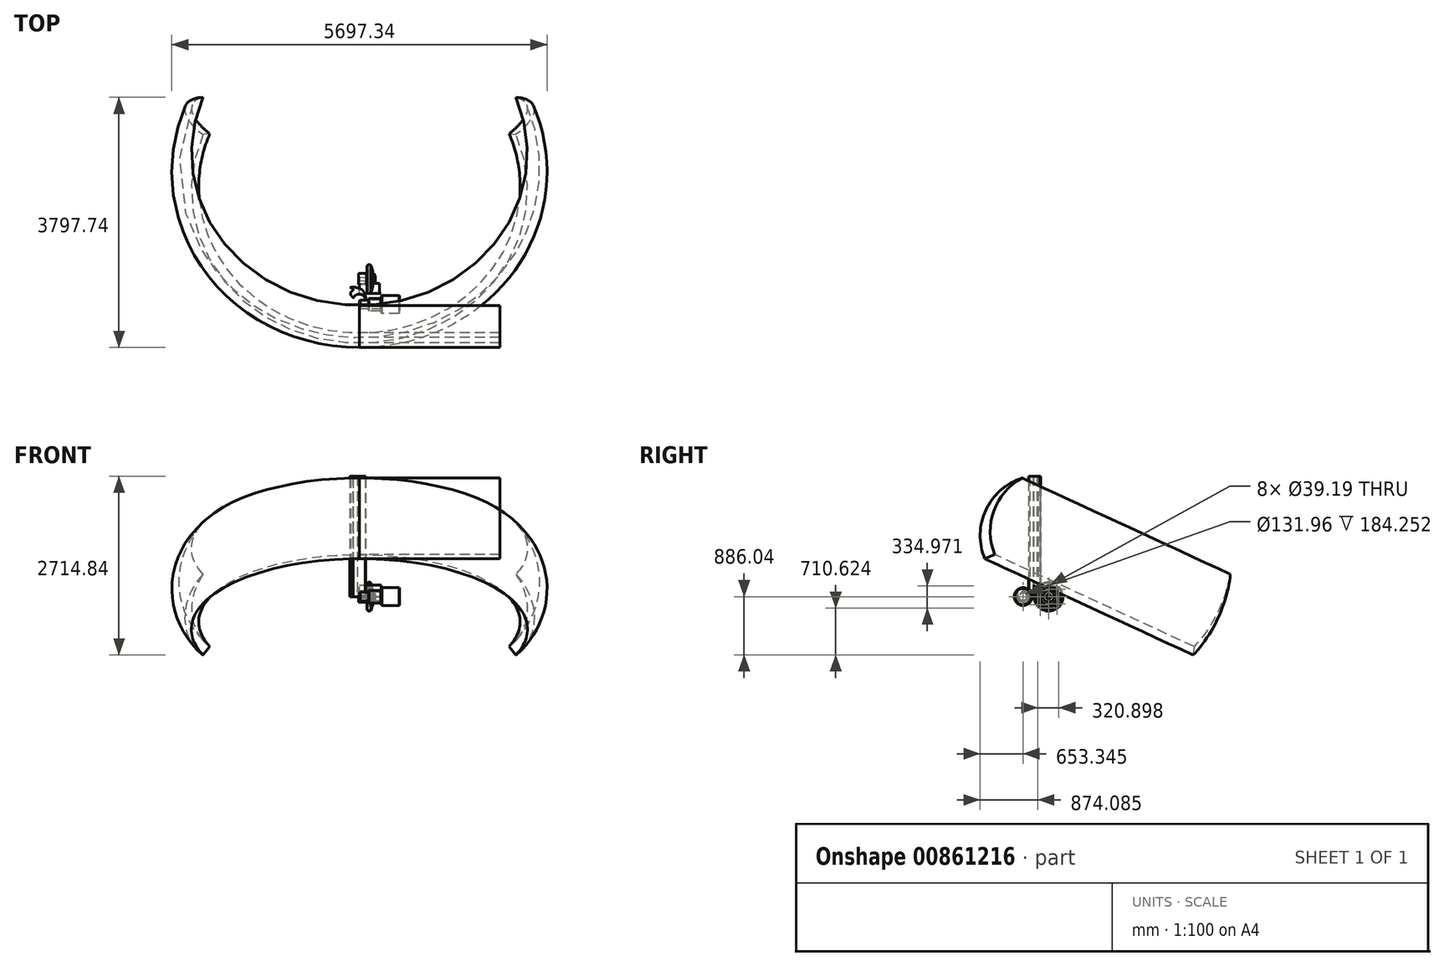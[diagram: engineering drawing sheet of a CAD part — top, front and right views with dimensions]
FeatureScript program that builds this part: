
annotation { "Feature Type Name" : "Feature", "Feature Type Description" : "" }
export const myFeature = defineFeature(function(context is Context, id is Id, definition is map)
    precondition{}
    {
        {
            var Q0;
            Q0=qCreatedBy(makeId("Top.planeOp"),FACE);
            var sketch = newSketch(context, id + "F0", { "sketchPlane" : qUnion([Q0])});
            skArc(sketch, "E0", {"start": v(158.63, -6.71) * mm, "mid": v(141.77, 43.9) * mm, "end": v(115.96, 90.57) * mm});
            skArc(sketch, "E1", {"start": v(-102.7, 32.7) * mm, "mid": v(-95.96, 50.16) * mm, "end": v(-88, 67.1) * mm});
            skArc(sketch, "E2", {"start": v(32.26, -37.2) * mm, "mid": v(37.68, -43.96) * mm, "end": v(39.61, -52.4) * mm});
            skArc(sketch, "E3", {"start": v(69.93, 27.33) * mm, "mid": v(43.86, 47.46) * mm, "end": v(12.76, 36.58) * mm});
            skArc(sketch, "E4", {"start": v(-33.84, 81.38) * mm, "mid": v(66.44, 22.45) * mm, "end": v(89.54, -91.55) * mm});
            skArc(sketch, "E5", {"start": v(0, 0) * mm, "mid": v(7.43, -55.42) * mm, "end": v(-5.4, -109.85) * mm});
            skArc(sketch, "E6", {"start": v(89.54, -91.55) * mm, "mid": v(5.41, -13.78) * mm, "end": v(-93.9, -70.91) * mm});
            skArc(sketch, "E7", {"start": v(-33.84, 81.38) * mm, "mid": v(-88.84, 92.71) * mm, "end": v(-144.42, 84.8) * mm});
            skArc(sketch, "E8", {"start": v(-93.9, -70.91) * mm, "mid": v(-127.37, -29.14) * mm, "end": v(-150.5, 19.13) * mm});
            skArc(sketch, "E9", {"start": v(-144.42, 84.8) * mm, "mid": v(-115.75, 75.17) * mm, "end": v(-94.38, 53.76) * mm});
            skArc(sketch, "E10", {"start": v(-100.08, 39.93) * mm, "mid": v(-128.56, 17.02) * mm, "end": v(-133.27, -19.23) * mm});
            skSolve(sketch);
        }
        {
            var Q0;
            Q0 = qSketchRegion(id + "F0", true);
            extrude(context, id + "F1", {"entities" : qUnion([Q0]), "depth" : 1828.8 * mm, "offsetDistance" : 25.4 * mm});
        }
        {
            var Q0;
            Q0=qCreatedBy(makeId("Right.planeOp"),FACE);
            var sketch = newSketch(context, id + "F2", { "sketchPlane" : qUnion([Q0])});
            skArc(sketch, "E11", {"start": v(-87.43, 1824.58) * mm, "mid": v(-731.28, 1330.32) * mm, "end": v(-728.31, 518.64) * mm});
            skArc(sketch, "E12", {"start": v(101, 1894.76) * mm, "mid": v(-605, 1335.85) * mm, "end": v(-489.64, 442.82) * mm});
            skLineSegment(sketch, "E13", {"start": v(798.75, 1224.43) * mm, "end": v(-1731.57, 164.88) * mm});
            skLineSegment(sketch, "E14", {"start": v(2827.78, 2242.44) * mm, "end": v(970.67, -1777.5) * mm});
            skSolve(sketch);
        }
        {
            var Q0;
            Q0 = qSketchRegion(id + "F2", true);
            extrude(context, id + "F3", {"entities" : qUnion([Q0]), "depth" : 2133.6 * mm, "offsetDistance" : 25.4 * mm});
        }
        {
            var Q0;
            Q0=qCreatedBy(makeId("Top.planeOp"),FACE);
            var sketch = newSketch(context, id + "F4", { "sketchPlane" : qUnion([Q0])});
            skArc(sketch, "E15", {"start": v(121.6, 54.3) * mm, "mid": v(126.73, 2.62) * mm, "end": v(177.93, 11.34) * mm});
            skLineSegment(sketch, "E16", {"start": v(121.6, 54.3) * mm, "end": v(148.26, 30.86) * mm});
            skLineSegment(sketch, "E17", {"start": v(177.93, 11.34) * mm, "end": v(177.93, 11.34) * mm});
            skLineSegment(sketch, "E18", {"start": v(148.26, 30.86) * mm, "end": v(177.93, 11.34) * mm});
            skLineSegment(sketch, "E19", {"start": v(200.93, 88.42) * mm, "end": v(121.6, 54.3) * mm});
            skLineSegment(sketch, "E20", {"start": v(200.93, 88.42) * mm, "end": v(177.93, 11.34) * mm});
            skLineSegment(sketch, "E21", {"start": v(-13.98, 128.72) * mm, "end": v(107.32, 128.72) * mm});
            skLineSegment(sketch, "E22", {"start": v(107.32, 128.72) * mm, "end": v(123.43, 88.86) * mm});
            skLineSegment(sketch, "E23", {"start": v(123.43, 88.86) * mm, "end": v(137.37, 130.58) * mm});
            skLineSegment(sketch, "E24", {"start": v(137.37, 130.58) * mm, "end": v(220.37, 130.58) * mm});
            skLineSegment(sketch, "E25", {"start": v(220.37, 130.58) * mm, "end": v(239.27, 177.24) * mm});
            skLineSegment(sketch, "E26", {"start": v(239.27, 177.24) * mm, "end": v(0, 193.5) * mm});
            skLineSegment(sketch, "E27", {"start": v(0, 193.5) * mm, "end": v(-13.98, 128.72) * mm});
            skLineSegment(sketch, "E28", {"start": v(-20.32, 214.6) * mm, "end": v(278.68, 214.6) * mm, "construction": true});
            skSolve(sketch);
        }
        {
            var Q0;
            Q0 = qSketchRegion(id + "F4", true);
            var Q1;
            Q1=sQuery(id+"F4.wireOp",EDGE,"E28");
            revolve(context, id + "F5", {"surfaceOperationType" : NewSurfaceOperationType.NEW, "entities" : qUnion([Q0]), "axis" : qUnion([Q1]), "revolveType" : RevolveType.FULL});
        }
        {
            var Q0;
            Q0=qCreatedBy(makeId("Right.planeOp"),FACE);
            var sketch = newSketch(context, id + "F6", { "sketchPlane" : qUnion([Q0])});
            skPoint(sketch, "E29", {"position": v(223.87, 159.55) * mm});
            skPoint(sketch, "E30", {"position": v(217.65, -175.42) * mm});
            skPoint(sketch, "E31", {"position": v(370.18, 0) * mm});
            skPoint(sketch, "E32", {"position": v(49.28, 0) * mm});
            skPoint(sketch, "E33", {"position": v(85.34, 94.38) * mm});
            skPoint(sketch, "E34", {"position": v(340.6, -108.3) * mm});
            skPoint(sketch, "E35", {"position": v(337.5, 108.16) * mm});
            skPoint(sketch, "E36", {"position": v(90.01, -123.2) * mm});
            skSolve(sketch);
        }
        {
            var Q0;
            Q0=sQuery(id+"F6.wireOp",VERTEX,"E31");
            var Q1;
            Q1=sQuery(id+"F6.wireOp",VERTEX,"E34");
            var Q2;
            Q2=sQuery(id+"F6.wireOp",VERTEX,"E30");
            var Q3;
            Q3=sQuery(id+"F6.wireOp",VERTEX,"E29");
            var Q4;
            Q4=sQuery(id+"F6.wireOp",VERTEX,"E33");
            var Q5;
            Q5=sQuery(id+"F6.wireOp",VERTEX,"E32");
            var Q6;
            Q6=sQuery(id+"F6.wireOp",VERTEX,"E36");
            var Q7;
            Q7=sQuery(id+"F6.wireOp",VERTEX,"E35");
            var Q8;
            Q8=makeQuery(id+"F5.opRevolve","SWEPT_BODY",BODY,{"disambiguationData":[OSD([sQuery(id+"F4.wireOp",EDGE,"E15"),sQuery(id+"F4.wireOp",EDGE,"E19"),sQuery(id+"F4.wireOp",EDGE,"E20")])]});
            hole(context, id + "F7", {"style" : HoleStyle.SIMPLE, "endStyle" : HoleEndStyle.THROUGH, "oppositeDirection" : true, "holeDiameter" : 39.2 * mm, "majorDiameter" : 6.35 * mm, "isTappedThrough" : true, "tappedDepth" : 12.7 * mm, "tapClearance" : 3, "locations" : qUnion([Q0, Q1, Q2, Q3, Q4, Q5, Q6, Q7]), "scope" : qUnion([Q8])});
        }
        {
            var Q0;
            Q0=qCreatedBy(makeId("Top.planeOp"),FACE);
            var sketch = newSketch(context, id + "F8", { "sketchPlane" : qUnion([Q0])});
            skLineSegment(sketch, "E37.bottom", {"start": v(0, 0) * mm, "end": v(304.8, 0) * mm});
            skLineSegment(sketch, "E37.top", {"start": v(0, 152.4) * mm, "end": v(304.8, 152.4) * mm});
            skLineSegment(sketch, "E37.left", {"start": v(0, 0) * mm, "end": v(0, 152.4) * mm});
            skLineSegment(sketch, "E37.right", {"start": v(304.8, 0) * mm, "end": v(304.8, 152.4) * mm});
            skSolve(sketch);
        }
        {
            var Q0;
            Q0 = qSketchRegion(id + "F8", true);
            extrude(context, id + "F9", {"entities" : qUnion([Q0]), "depth" : (12 * (1 / 3)) * mm, "offsetDistance" : 25.4 * mm});
        }
        {
            var Q0;
            Q0=qCreatedBy(makeId("Front.planeOp"),FACE);
            var sketch = newSketch(context, id + "F10", { "sketchPlane" : qUnion([Q0])});
            skLineSegment(sketch, "E38.bottom", {"start": v(0, 0) * mm, "end": v(330.2, 0) * mm});
            skLineSegment(sketch, "E38.top", {"start": v(0, 177.8) * mm, "end": v(330.2, 177.8) * mm});
            skLineSegment(sketch, "E38.left", {"start": v(0, 0) * mm, "end": v(0, 177.8) * mm});
            skLineSegment(sketch, "E38.right", {"start": v(330.2, 0) * mm, "end": v(330.2, 177.8) * mm});
            skSolve(sketch);
        }
        {
            var Q0;
            Q0 = qSketchRegion(id + "F10", true);
            extrude(context, id + "F11", {"entities" : qUnion([Q0]), "depth" : ((12 * (1 / 3)) + 1) * mm, "offsetDistance" : 25.4 * mm});
        }
        {
            var Q0;
            {var subQ0=sQuery(id+"F2.wireOp",EDGE,"E12");var subQ1=sQuery(id+"F2.wireOp",EDGE,"E11");var subQ2=makeQuery(id+"F2.imprint","INTERSECT",VERTEX,{"derivedFrom":[subQ1,subQ0]});Q0=makeQuery(id+"F2.imprint","IMPRINT",FACE,{"disambiguationData":[TD([[makeQuery(id+"F2.imprint","IMPRINT",EDGE,{"disambiguationData":[TD([[subQ2,-1.0]])],"derivedFrom":subQ1}),1.0]])]});}
            var Q1;
            Q1=sQuery(id+"F2.wireOp",EDGE,"E14");
            revolve(context, id + "F12", {"surfaceOperationType" : NewSurfaceOperationType.NEW, "entities" : qUnion([Q0]), "axis" : qUnion([Q1]), "revolveType" : RevolveType.SYMMETRIC, "angle" : 222.76 * degree});
        }
        {
            var Q0;
            Q0=qCreatedBy(makeId("Right.planeOp"),FACE);
            var sketch = newSketch(context, id + "F13", { "sketchPlane" : qUnion([Q0])});
            skCircle(sketch, "E39", {"center": v(-171.46, 0) * mm, "radius": 65.98 * mm});
            skSolve(sketch);
        }
        {
            var Q0;
            Q0 = qSketchRegion(id + "F13", true);
            extrude(context, id + "F14", {"entities" : qUnion([Q0]), "depth" : 137.98 * mm, "offsetDistance" : 25.4 * mm});
        }
        {
            var Q0;
            Q0=makeQuery(id+"F14.opExtrude","CAP_FACE",FACE,{"disambiguationData":[OSD([sQuery(id+"F13.wireOp",EDGE,"E39")])],"isStart":false});
            var sketch = newSketch(context, id + "F15", { "sketchPlane" : qUnion([Q0])});
            skCircle(sketch, "E40", {"center": v(-171.46, 0) * mm, "radius": 95.24 * mm});
            skSolve(sketch);
        }
        {
            var Q0;
            Q0=makeQuery(id+"F15.imprint","IMPRINT",FACE,{"disambiguationData":[TD([[makeQuery(id+"F15.imprint","IMPRINT",EDGE,{"derivedFrom":sQuery(id+"F15.wireOp",EDGE,"E40")}),1.0]])]});
            extrude(context, id + "F16", {"entities" : qUnion([Q0]), "depth" : 194.4 * mm, "offsetDistance" : 25.4 * mm});
        }
        {
            var Q0;
            Q0=makeQuery(id+"F16.opExtrude","CAP_FACE",FACE,{"disambiguationData":[OSD([sQuery(id+"F13.wireOp",EDGE,"E39"),sQuery(id+"F15.wireOp",EDGE,"E40")])],"isStart":false});
            var sketch = newSketch(context, id + "F17", { "sketchPlane" : qUnion([Q0])});
            skCircle(sketch, "E41", {"center": v(-171.46, 0) * mm, "radius": 135.39 * mm});
            skSolve(sketch);
        }
        {
            var Q0;
            Q0 = qSketchRegion(id + "F17", true);
            extrude(context, id + "F18", {"entities" : qUnion([Q0]), "depth" : 279.07 * mm, "offsetDistance" : 25.4 * mm});
        }
        {
            var Q0;
            Q0=makeQuery(id+"F18.opExtrude","CAP_EDGE",EDGE,{"disambiguationData":[OSD([sQuery(id+"F17.wireOp",EDGE,"E41")])],"isStart":false});
            var Q1;
            Q1=makeQuery(id+"F18.opExtrude","CAP_EDGE",EDGE,{"disambiguationData":[OSD([sQuery(id+"F17.wireOp",EDGE,"E41")])],"isStart":true});
            var Q2;
            Q2=makeQuery(id+"F16.opExtrude","CAP_EDGE",EDGE,{"disambiguationData":[OSD([sQuery(id+"F15.wireOp",EDGE,"E40")])],"isStart":true});
            var Q3;
            Q3=makeQuery(id+"F14.opExtrude","CAP_EDGE",EDGE,{"disambiguationData":[OSD([sQuery(id+"F13.wireOp",EDGE,"E39")])],"isStart":true});
            var Q4;
            Q4=makeQuery(id+"F16.opExtrude","CAP_EDGE",EDGE,{"disambiguationData":[OSD([sQuery(id+"F15.wireOp",EDGE,"E40")])],"isStart":false});
            var Q5;
            Q5=makeQuery(id+"F16.opExtrude","CAP_EDGE",EDGE,{"disambiguationData":[OSD([sQuery(id+"F13.wireOp",EDGE,"E39")])],"isStart":true});
            chamfer(context, id + "F19", {"entities" : qUnion([Q0, Q1, Q2, Q3, Q4, Q5]), "width" : 10.16 * mm, "tangentPropagation" : true});
        }
    });
